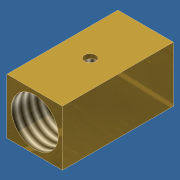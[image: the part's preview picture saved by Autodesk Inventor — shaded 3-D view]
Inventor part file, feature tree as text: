
AUTODESK INVENTOR PART (.ipt)
format: ipt  version: unknown  size: 178,688 bytes
history: native  units: in
note: dims shown in document units (in); Inventor stores cm internally (conversion verified against a paired STEP export)
features: extrude x2, sketch x2, thread x1
ambient origin geometry x8: Origin, YZ Plane, XZ Plane, XY Plane, X Axis, Y Axis, Z Axis, Center Point
bodies: Solid1 (feature_tree)
feature tree (5):
  extrude  "Extrusion1"  Depth=0.75in
  extrude  "Extrusion2"  Depth=1.5in TaperAngle=0.0deg
  thread  "Thread1"  [1 undecoded]
  sketch  "Sketch1"  dims[d0=0.75in d1=0.75in]
  sketch  "Sketch2"  dims[d2=0.425in d3=1.5in d4=0.0in d5=0.1in d6=0.25in d7=0.0in d8=1.0in d9=0.0in]
note: 1 required parameter value undecoded (feature->parameter linkage not recoverable at this tier; creation-order binding heuristic only, values carry confidence <= 0.55)
